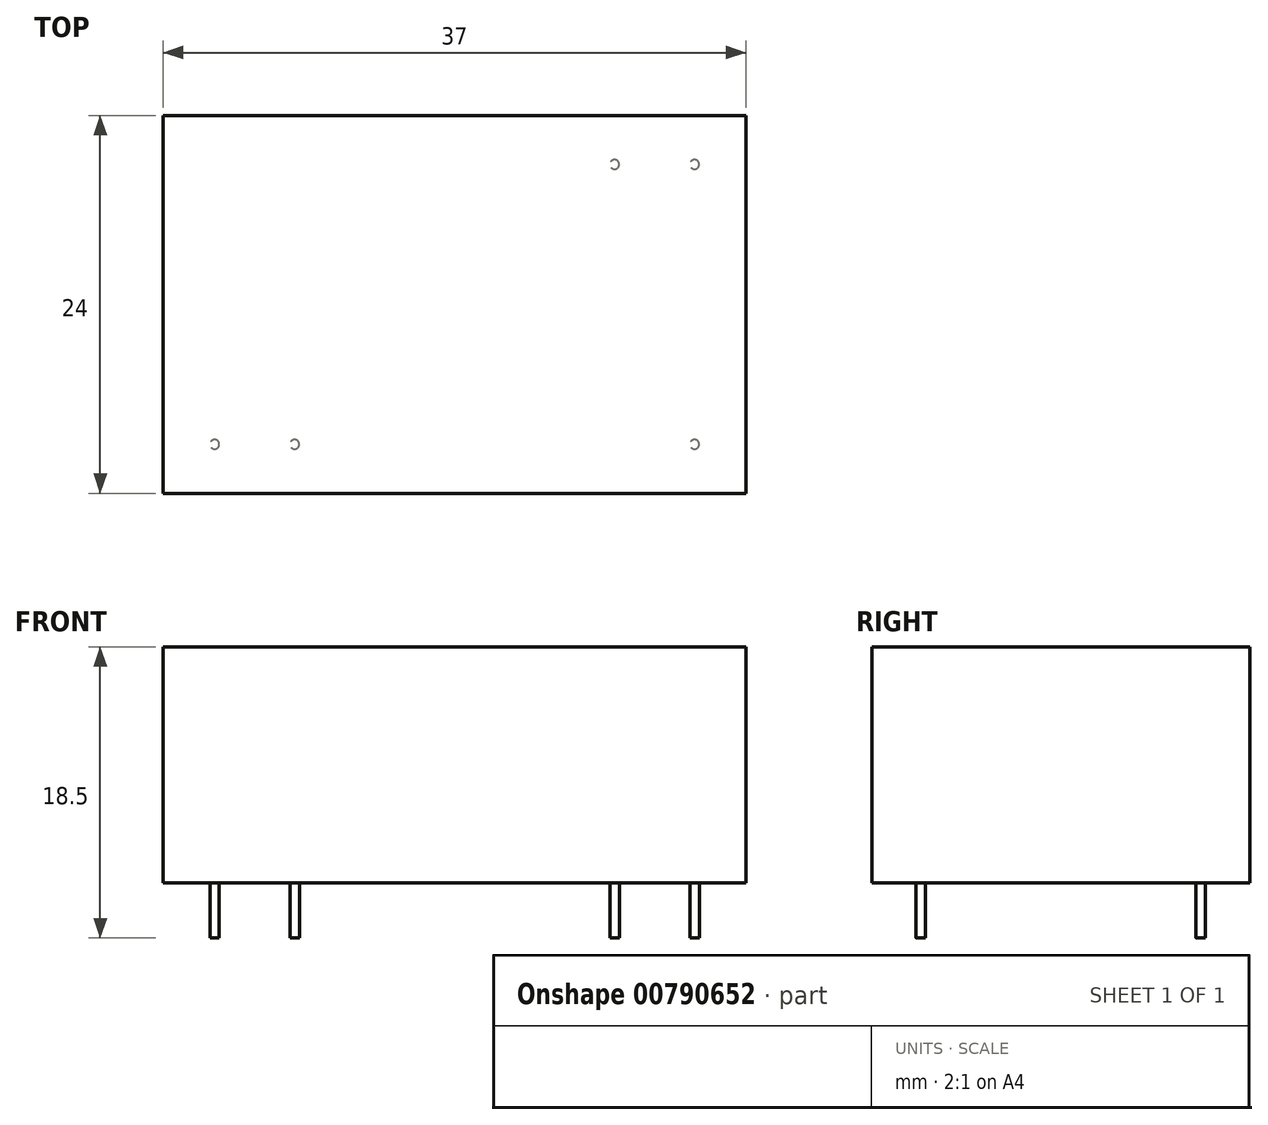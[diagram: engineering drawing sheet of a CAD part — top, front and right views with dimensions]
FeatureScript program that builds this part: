
annotation { "Feature Type Name" : "Feature", "Feature Type Description" : "" }
export const myFeature = defineFeature(function(context is Context, id is Id, definition is map)
    precondition{}
    {
        {
            var Q0;
            Q0=qCreatedBy(makeId("Top.planeOp"),FACE);
            var sketch = newSketch(context, id + "F0", { "sketchPlane" : qUnion([Q0])});
            skLineSegment(sketch, "E0.bottom", {"start": v(18.5, -12) * mm, "end": v(-18.5, -12) * mm});
            skLineSegment(sketch, "E0.top", {"start": v(18.5, 12) * mm, "end": v(-18.5, 12) * mm});
            skLineSegment(sketch, "E0.left", {"start": v(18.5, -12) * mm, "end": v(18.5, 12) * mm});
            skLineSegment(sketch, "E0.right", {"start": v(-18.5, -12) * mm, "end": v(-18.5, 12) * mm});
            skPoint(sketch, "E0.middle", {"position": v(0, 0) * mm});
            skPoint(sketch, "E1", {"position": v(-15.24, 8.89) * mm});
            skPoint(sketch, "E2", {"position": v(-10.16, 8.89) * mm});
            skPoint(sketch, "E3", {"position": v(15.24, 8.9) * mm});
            skPoint(sketch, "E4", {"position": v(15.24, -8.89) * mm});
            skPoint(sketch, "E5", {"position": v(10.16, -8.89) * mm});
            skCircle(sketch, "E6", {"center": v(-15.24, 8.89) * mm, "radius": 0.3 * mm});
            skCircle(sketch, "E7", {"center": v(-10.16, 8.89) * mm, "radius": 0.3 * mm});
            skCircle(sketch, "E8", {"center": v(15.24, 8.9) * mm, "radius": 0.3 * mm});
            skCircle(sketch, "E9", {"center": v(15.24, -8.89) * mm, "radius": 0.3 * mm});
            skCircle(sketch, "E10", {"center": v(10.16, -8.89) * mm, "radius": 0.3 * mm});
            skSolve(sketch);
        }
        {
            var Q0;
            Q0=makeQuery(id+"F0.imprint","IMPRINT",FACE,{"disambiguationData":[TD([[makeQuery(id+"F0.imprint","IMPRINT",EDGE,{"derivedFrom":sQuery(id+"F0.wireOp",EDGE,"E0.bottom")}),-1.0]])]});
            extrude(context, id + "F1", {"entities" : qUnion([Q0]), "depth" : 15 * mm, "offsetDistance" : 25 * mm});
        }
        {
            var Q0;
            Q0=makeQuery(id+"F0.imprint","IMPRINT",FACE,{"disambiguationData":[TD([[makeQuery(id+"F0.imprint","IMPRINT",EDGE,{"derivedFrom":sQuery(id+"F0.wireOp",EDGE,"E8")}),1.0]])]});
            var Q1;
            Q1=makeQuery(id+"F0.imprint","IMPRINT",FACE,{"disambiguationData":[TD([[makeQuery(id+"F0.imprint","IMPRINT",EDGE,{"derivedFrom":sQuery(id+"F0.wireOp",EDGE,"E7")}),1.0]])]});
            var Q2;
            Q2=makeQuery(id+"F0.imprint","IMPRINT",FACE,{"disambiguationData":[TD([[makeQuery(id+"F0.imprint","IMPRINT",EDGE,{"derivedFrom":sQuery(id+"F0.wireOp",EDGE,"E6")}),1.0]])]});
            var Q3;
            Q3=makeQuery(id+"F0.imprint","IMPRINT",FACE,{"disambiguationData":[TD([[makeQuery(id+"F0.imprint","IMPRINT",EDGE,{"derivedFrom":sQuery(id+"F0.wireOp",EDGE,"E9")}),1.0]])]});
            var Q4;
            Q4=makeQuery(id+"F0.imprint","IMPRINT",FACE,{"disambiguationData":[TD([[makeQuery(id+"F0.imprint","IMPRINT",EDGE,{"derivedFrom":sQuery(id+"F0.wireOp",EDGE,"E10")}),1.0]])]});
            extrude(context, id + "F2", {"entities" : qUnion([Q0, Q1, Q2, Q3, Q4]), "operationType" : NewBodyOperationType.ADD, "depth" : (15 + 3.5) * mm, "offsetDistance" : 25 * mm});
        }
        {
            var Q0;
            Q0=makeQuery(id+"F1.opExtrude","SWEPT_BODY",BODY,{"disambiguationData":[OSD([sQuery(id+"F0.wireOp",EDGE,"E0.bottom"),sQuery(id+"F0.wireOp",EDGE,"E0.top"),sQuery(id+"F0.wireOp",EDGE,"E0.left"),sQuery(id+"F0.wireOp",EDGE,"E0.right"),sQuery(id+"F0.wireOp",EDGE,"E6"),sQuery(id+"F0.wireOp",EDGE,"E7"),sQuery(id+"F0.wireOp",EDGE,"E8"),sQuery(id+"F0.wireOp",EDGE,"E9"),sQuery(id+"F0.wireOp",EDGE,"E10")])]});
            var Q1;
            Q1=makeQuery(id+"F1.opExtrude","CAP_EDGE",EDGE,{"disambiguationData":[OSD([sQuery(id+"F0.wireOp",EDGE,"E0.bottom")])],"isStart":false});
            transform(context, id + "F3", {"entities" : qUnion([Q0]), "transformType" : TransformType.ROTATION, "transformAxis" : qUnion([Q1]), "angle" : 180 * degree, "makeCopy" : false});
        }
    });
